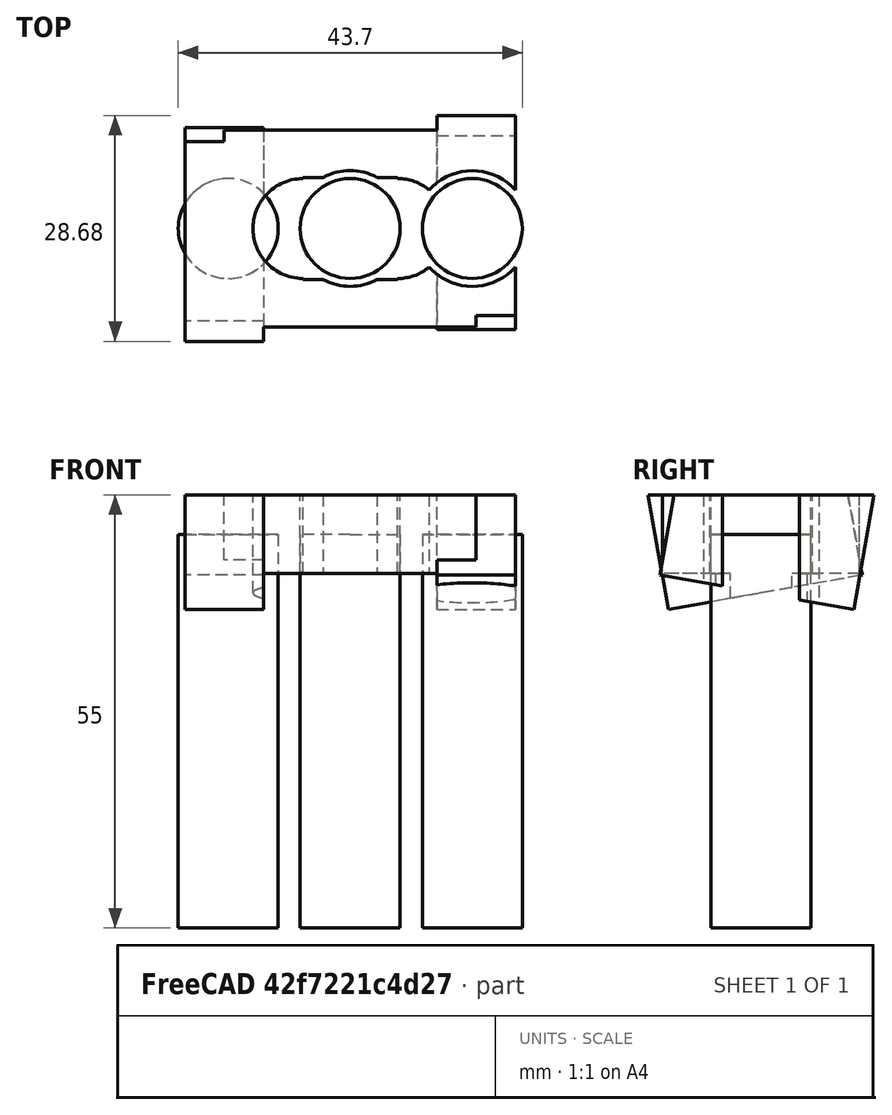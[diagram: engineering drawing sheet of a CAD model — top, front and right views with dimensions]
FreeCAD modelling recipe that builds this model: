
FCSTD DOCUMENT  (FreeCAD 0.20R29410 (Git))
Label: laddle1
License: All rights reserved
LicenseURL: http://en.wikipedia.org/wiki/All_rights_reserved
objects: Part::Cylinder×11, Part::MultiFuse×10, Part::Box×6, Part::Cut×4, Part::Feature×1
note: 32 computed .brp shape members not serialized (recipe doc carries the construction recipe); baked Part::Feature solids carry a one-line shape summary decoded from their .brp

FEATURE [Part::Box] Box065  label="Cube065"
  AttacherType = Attacher::AttachEngine3D
  Height = 20
  Length = 10
  Placement = pos=(11,-12.8391,44.8084) rot=(-1,0,0;0.174533rad)
  Width = 25
FEATURE [Part::Box] Box066  label="Cube066"
  AttacherType = Attacher::AttachEngine3D
  Height = 20
  Length = 10
  Placement = pos=(11,-12.8391,44.8084) rot=(-1,0,0;0.174533rad)
  Width = 25
FEATURE [Part::Cylinder] Cylinder003  label="bevilPin"
  Angle = 360
  AttacherType = Attacher::AttachEngine3D
  FirstAngle = 0
  Height = 55
  Radius = 6.35
  SecondAngle = 0
FEATURE [Part::Box] Box  label="Cube"
  AttacherType = Attacher::AttachEngine3D
  Height = 10
  Length = 32
  Placement = pos=(-16,-12.5,45) rot=(0,0,1;0rad)
  Width = 25
FEATURE [Part::Cylinder] Cylinder049  label="bevilPin036"
  Angle = 360
  AttacherType = Attacher::AttachEngine3D
  FirstAngle = 0
  Height = 55
  Radius = 6.35
  SecondAngle = 0
FEATURE [Part::Cylinder] Cylinder048  label="bevilPin035"
  Angle = 360
  AttacherType = Attacher::AttachEngine3D
  FirstAngle = 0
  Height = 55
  Radius = 6.35
  SecondAngle = 0
FEATURE [Part::MultiFuse] Fusion096
  Shapes = -> [Cylinder048,Box065]
FEATURE [Part::MultiFuse] Fusion097
  Placement = pos=(0,0,0) rot=(0,0,1;3.14159rad)
  Shapes = -> [Cylinder049,Box066]
FEATURE [Part::Box] Box067  label="Cube067"
  AttacherType = Attacher::AttachEngine3D
  Height = 10
  Length = 62
  Placement = pos=(-27,-21.5,55) rot=(0,0,1;0rad)
  Width = 55
FEATURE [Part::MultiFuse] Fusion
  Shapes = -> [Box,Fusion097]
FEATURE [Part::MultiFuse] Fusion098
  Shapes = -> [Fusion096,Fusion]
FEATURE [Part::Cut] Cut
  Base = -> Fusion098
  Tool = -> Box067
FEATURE [Part::Cylinder] Cylinder050  label="bevilPin037"
  Angle = 360
  AttacherType = Attacher::AttachEngine3D
  FirstAngle = 0
  Height = 55
  Radius = 7.35
  SecondAngle = 0
FEATURE [Part::Cylinder] Cylinder006
  Angle = 360
  AttacherType = Attacher::AttachEngine3D
  FirstAngle = 0
  Height = 50
  Placement = pos=(0,15.5,0) rot=(0,0,1;0rad)
  Radius = 6.35
  SecondAngle = 0
FEATURE [Part::Cylinder] Cylinder007
  Angle = 360
  AttacherType = Attacher::AttachEngine3D
  FirstAngle = 0
  Height = 50
  Radius = 6.35
  SecondAngle = 0
FEATURE [Part::Cylinder] Cylinder008
  Angle = 360
  AttacherType = Attacher::AttachEngine3D
  FirstAngle = 0
  Height = 50
  Placement = pos=(0,15.5,0) rot=(0,0,1;0rad)
  Radius = 6.35
  SecondAngle = 0
FEATURE [Part::Cylinder] Cylinder009
  Angle = 360
  AttacherType = Attacher::AttachEngine3D
  FirstAngle = 0
  Height = 50
  Radius = 6.35
  SecondAngle = 0
FEATURE [Part::MultiFuse] Fusion003
  Shapes = -> [Cylinder006,Cylinder007]
FEATURE [Part::MultiFuse] Fusion004
  Placement = pos=(0,0,0) rot=(0,0,1;3.14159rad)
  Shapes = -> [Cylinder008,Cylinder009]
FEATURE [Part::MultiFuse] Fusion005
  Placement = pos=(0,0,0) rot=(0,0,1;4.71239rad)
  Shapes = -> [Fusion004,Fusion003]
FEATURE [Part::Cylinder] Cylinder
  Angle = 360
  AttacherType = Attacher::AttachEngine3D
  FirstAngle = 0
  Height = 60
  Placement = pos=(15.5,0,0) rot=(0,0,1;0rad)
  Radius = 7.35
  SecondAngle = 0
FEATURE [Part::Cut] Cut001
  Base = -> Cut
  Tool = -> Cylinder
FEATURE [Part::Cut] Cut002
  Base = -> Cut001
  Tool = -> Cylinder050
FEATURE [Part::Cylinder] Cylinder051  label="bevilPin038"
  Angle = 360
  AttacherType = Attacher::AttachEngine3D
  FirstAngle = 0
  Height = 55
  Placement = pos=(6,0,0) rot=(0,0,1;0rad)
  Radius = 6.35
  SecondAngle = 0
FEATURE [Part::Box] Box068  label="Cube068"
  AttacherType = Attacher::AttachEngine3D
  Height = 55
  Length = 6
  Placement = pos=(0,-6.5,0) rot=(0,0,1;0rad)
  Width = 13
FEATURE [Part::MultiFuse] Fusion099
  Shapes = -> [Cylinder051,Box068]
FEATURE [Part::Box] Box069  label="Cube069"
  AttacherType = Attacher::AttachEngine3D
  Height = 55
  Length = 6
  Placement = pos=(0,-6.5,0) rot=(0,0,1;0rad)
  Width = 13
FEATURE [Part::Cylinder] Cylinder052  label="bevilPin039"
  Angle = 360
  AttacherType = Attacher::AttachEngine3D
  FirstAngle = 0
  Height = 55
  Placement = pos=(6,0,0) rot=(0,0,1;0rad)
  Radius = 6.35
  SecondAngle = 0
FEATURE [Part::MultiFuse] Fusion100
  Placement = pos=(0,0,0) rot=(0,0,1;3.14159rad)
  Shapes = -> [Cylinder052,Box069]
FEATURE [Part::MultiFuse] Fusion101
  Shapes = -> [Fusion100,Fusion099]
FEATURE [Part::Cut] Cut003
  Base = -> Cut002
  Tool = -> Fusion101
FEATURE [Part::Feature] Cut003_solid  label="Cut003 (Solid)"
  shape: bbox 42 x 28.69 x 14.53 mm, 41 faces (baked)
